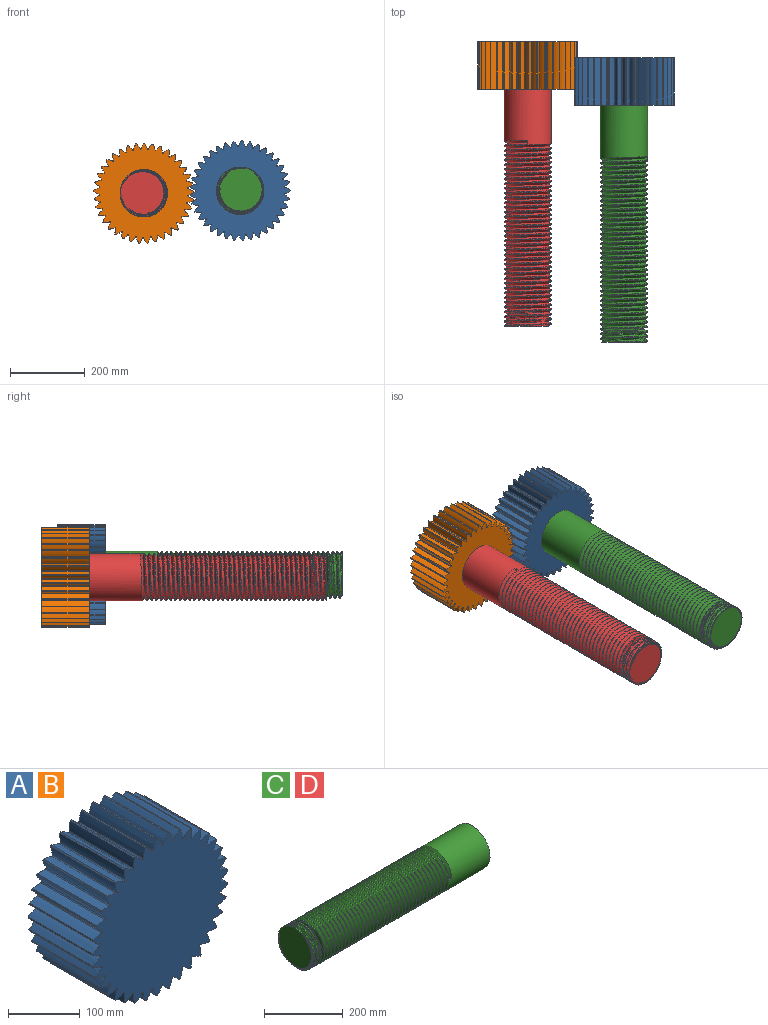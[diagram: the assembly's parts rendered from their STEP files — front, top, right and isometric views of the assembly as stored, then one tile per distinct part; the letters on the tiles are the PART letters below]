
ASSEMBLY  parts=4 mates=2
PART A: 150 faces, bbox 267.3x127x267.6 mm
  f0: cylinder r=133.86mm len=127mm, axis (0,1,0), area 302.8mm2, adj f139,f146,f148,f149
  f1: cylinder r=133.86mm len=127mm, axis (0,1,0), area 302.8mm2, adj f143,f145,f148,f149
  f2: cylinder r=133.86mm len=127mm, axis (0,1,0), area 302.8mm2, adj f136,f140,f148,f149
  f3: cylinder r=133.86mm len=127mm, axis (0,1,0), area 302.8mm2, adj f133,f137,f148,f149
  f4: cylinder r=133.86mm len=127mm, axis (0,1,0), area 302.8mm2, adj f130,f134,f148,f149
  f5: cylinder r=133.86mm len=127mm, axis (0,1,0), area 302.8mm2, adj f127,f131,f148,f149
  f6: cylinder r=133.86mm len=127mm, axis (0,1,0), area 302.8mm2, adj f124,f128,f148,f149
  f7: cylinder r=133.86mm len=127mm, axis (0,1,0), area 302.8mm2, adj f115,f125,f148,f149
  f8: cylinder r=133.86mm len=127mm, axis (0,1,0), area 302.8mm2, adj f109,f122,f148,f149
  f9: cylinder r=133.86mm len=127mm, axis (0,1,0), area 302.8mm2, adj f119,f121,f148,f149
  f10: cylinder r=133.86mm len=127mm, axis (0,1,0), area 302.8mm2, adj f112,f116,f148,f149
  f11: cylinder r=133.86mm len=127mm, axis (0,1,0), area 302.8mm2, adj f113,f118,f148,f149
  f12: cylinder r=133.86mm len=127mm, axis (0,1,0), area 302.8mm2, adj f106,f110,f148,f149
  f13: cylinder r=133.86mm len=127mm, axis (0,1,0), area 302.8mm2, adj f103,f107,f148,f149
  f14: cylinder r=133.86mm len=127mm, axis (0,1,0), area 302.8mm2, adj f100,f104,f148,f149
  f15: cylinder r=133.86mm len=127mm, axis (0,1,0), area 302.8mm2, adj f88,f101,f148,f149
  f16: cylinder r=133.86mm len=127mm, axis (0,1,0), area 302.8mm2, adj f94,f98,f148,f149
  f17: cylinder r=133.86mm len=127mm, axis (0,1,0), area 302.8mm2, adj f85,f95,f148,f149
  f18: cylinder r=133.86mm len=127mm, axis (0,1,0), area 302.8mm2, adj f92,f97,f148,f149
  f19: cylinder r=133.86mm len=127mm, axis (0,1,0), area 302.8mm2, adj f89,f91,f148,f149
  f20: cylinder r=133.86mm len=127mm, axis (0,1,0), area 302.8mm2, adj f82,f86,f148,f149
  f21: cylinder r=133.86mm len=127mm, axis (0,1,0), area 302.8mm2, adj f79,f83,f148,f149
  f22: cylinder r=133.86mm len=127mm, axis (0,1,0), area 302.8mm2, adj f76,f80,f148,f149
  f23: cylinder r=133.86mm len=127mm, axis (0,1,0), area 302.8mm2, adj f52,f77,f148,f149
  f24: cylinder r=133.86mm len=127mm, axis (0,1,0), area 302.8mm2, adj f37,f74,f148,f149
  f25: cylinder r=133.86mm len=127mm, axis (0,1,0), area 302.8mm2, adj f71,f73,f148,f149
  f26: cylinder r=133.86mm len=127mm, axis (0,1,0), area 302.8mm2, adj f64,f68,f148,f149
  f27: cylinder r=133.86mm len=127mm, axis (0,1,0), area 302.8mm2, adj f65,f70,f148,f149
  f28: cylinder r=133.86mm len=127mm, axis (0,1,0), area 302.8mm2, adj f58,f62,f148,f149
  f29: cylinder r=133.86mm len=127mm, axis (0,1,0), area 302.8mm2, adj f59,f67,f148,f149
  f30: cylinder r=133.86mm len=127mm, axis (0,1,0), area 302.8mm2, adj f56,f61,f148,f149
  f31: cylinder r=133.86mm len=127mm, axis (0,1,0), area 302.8mm2, adj f53,f55,f148,f149
  f32: cylinder r=133.86mm len=127mm, axis (0,1,0), area 302.8mm2, adj f46,f50,f148,f149
  f33: cylinder r=133.86mm len=127mm, axis (0,1,0), area 302.8mm2, adj f47,f142,f148,f149
  f34: cylinder r=133.86mm len=127mm, axis (0,1,0), area 302.8mm2, adj f44,f49,f148,f149
  f35: cylinder r=133.86mm len=127mm, axis (0,1,0), area 302.8mm2, adj f41,f43,f148,f149
  f36: cylinder r=133.86mm len=127mm, axis (0,1,0), area 302.8mm2, adj f38,f40,f148,f149
  f37: extruded ~127x14.19mm, area 2130.1mm2, adj f24,f39,f148,f149
  f38: extruded ~127x14.19mm, area 2130.1mm2, adj f36,f39,f148,f149
  f39: cylinder r=1.44mm len=127mm, axis (0,1,0), area 425.2mm2, adj f37,f38,f148,f149
  f40: extruded ~127x15.48mm, area 2130.1mm2, adj f36,f42,f148,f149
  f41: extruded ~127x12.49mm, area 2130.1mm2, adj f35,f42,f148,f149
  f42: cylinder r=1.44mm len=127mm, axis (0,1,0), area 425.2mm2, adj f40,f41,f148,f149
  f43: extruded ~127x16.33mm, area 2130.1mm2, adj f35,f45,f148,f149
  f44: extruded ~127x13.07mm, area 2130.1mm2, adj f34,f45,f148,f149
  f45: cylinder r=1.44mm len=127mm, axis (0,1,0), area 425.2mm2, adj f43,f44,f148,f149
  f46: extruded ~127x16.6mm, area 2130.1mm2, adj f32,f48,f148,f149
  f47: extruded ~127x15.8mm, area 2130.1mm2, adj f33,f48,f148,f149
  f48: cylinder r=1.44mm len=127mm, axis (0,1,0), area 425.2mm2, adj f46,f47,f148,f149
  f49: extruded ~127x16.7mm, area 2130.1mm2, adj f34,f51,f148,f149
  f50: extruded ~127x14.64mm, area 2130.1mm2, adj f32,f51,f148,f149
  f51: cylinder r=1.44mm len=127mm, axis (0,1,0), area 425.2mm2, adj f49,f50,f148,f149
  f52: extruded ~127x15.74mm, area 2130.1mm2, adj f23,f54,f148,f149
  f53: extruded ~127x12.01mm, area 2130.1mm2, adj f31,f54,f148,f149
  f54: cylinder r=1.44mm len=127mm, axis (0,1,0), area 425.2mm2, adj f52,f53,f148,f149
  f55: extruded ~127x16.47mm, area 2130.1mm2, adj f31,f57,f148,f149
  f56: extruded ~127x13.5mm, area 2130.1mm2, adj f30,f57,f148,f149
  f57: cylinder r=1.44mm len=127mm, axis (0,1,0), area 425.2mm2, adj f55,f56,f148,f149
  f58: extruded ~127x16.5mm, area 2130.1mm2, adj f28,f60,f148,f149
  f59: extruded ~127x16.01mm, area 2130.1mm2, adj f29,f60,f148,f149
  f60: cylinder r=1.44mm len=127mm, axis (0,1,0), area 425.2mm2, adj f58,f59,f148,f149
  f61: extruded ~127x16.72mm, area 2130.1mm2, adj f30,f63,f148,f149
  f62: extruded ~127x14.97mm, area 2130.1mm2, adj f28,f63,f148,f149
  f63: cylinder r=1.44mm len=127mm, axis (0,1,0), area 425.2mm2, adj f61,f62,f148,f149
  f64: extruded ~127x14.64mm, area 2130.1mm2, adj f26,f66,f148,f149
  f65: extruded ~127x16.7mm, area 2130.1mm2, adj f27,f66,f148,f149
  f66: cylinder r=1.44mm len=127mm, axis (0,1,0), area 425.2mm2, adj f64,f65,f148,f149
  f67: extruded ~127x15.8mm, area 2130.1mm2, adj f29,f69,f148,f149
  f68: extruded ~127x16.6mm, area 2130.1mm2, adj f26,f69,f148,f149
  f69: cylinder r=1.44mm len=127mm, axis (0,1,0), area 425.2mm2, adj f67,f68,f148,f149
  f70: extruded ~127x13.07mm, area 2130.1mm2, adj f27,f72,f148,f149
  f71: extruded ~127x16.33mm, area 2130.1mm2, adj f25,f72,f148,f149
  f72: cylinder r=1.44mm len=127mm, axis (0,1,0), area 425.2mm2, adj f70,f71,f148,f149
  f73: extruded ~127x12.49mm, area 2130.1mm2, adj f25,f75,f148,f149
  f74: extruded ~127x15.48mm, area 2130.1mm2, adj f24,f75,f148,f149
  f75: cylinder r=1.44mm len=127mm, axis (0,1,0), area 425.2mm2, adj f73,f74,f148,f149
  f76: extruded ~127x14.55mm, area 2130.1mm2, adj f22,f78,f148,f149
  f77: extruded ~127x13.8mm, area 2130.1mm2, adj f23,f78,f148,f149
  f78: cylinder r=1.44mm len=127mm, axis (0,1,0), area 425.2mm2, adj f76,f77,f148,f149
  f79: extruded ~127x12.95mm, area 2130.1mm2, adj f21,f81,f148,f149
  f80: extruded ~127x15.2mm, area 2130.1mm2, adj f22,f81,f148,f149
  f81: cylinder r=1.44mm len=127mm, axis (0,1,0), area 425.2mm2, adj f79,f80,f148,f149
  f82: extruded ~127x12.61mm, area 2130.1mm2, adj f20,f84,f148,f149
  f83: extruded ~127x16.16mm, area 2130.1mm2, adj f21,f84,f148,f149
  f84: cylinder r=1.44mm len=127mm, axis (0,1,0), area 425.2mm2, adj f82,f83,f148,f149
  f85: extruded ~127x14.28mm, area 2130.1mm2, adj f17,f87,f148,f149
  f86: extruded ~127x16.65mm, area 2130.1mm2, adj f20,f87,f148,f149
  f87: cylinder r=1.44mm len=127mm, axis (0,1,0), area 425.2mm2, adj f85,f86,f148,f149
  f88: extruded ~127x16.57mm, area 2130.1mm2, adj f15,f90,f148,f149
  f89: extruded ~127x13.9mm, area 2130.1mm2, adj f19,f90,f148,f149
  f90: cylinder r=1.44mm len=127mm, axis (0,1,0), area 425.2mm2, adj f88,f89,f148,f149
  f91: extruded ~127x16.71mm, area 2130.1mm2, adj f19,f93,f148,f149
  f92: extruded ~127x15.27mm, area 2130.1mm2, adj f18,f93,f148,f149
  f93: cylinder r=1.44mm len=127mm, axis (0,1,0), area 425.2mm2, adj f91,f92,f148,f149
  f94: extruded ~127x15.55mm, area 2130.1mm2, adj f16,f96,f148,f149
  f95: extruded ~127x16.67mm, area 2130.1mm2, adj f17,f96,f148,f149
  f96: cylinder r=1.44mm len=127mm, axis (0,1,0), area 425.2mm2, adj f94,f95,f148,f149
  f97: extruded ~127x16.36mm, area 2130.1mm2, adj f18,f99,f148,f149
  f98: extruded ~127x16.2mm, area 2130.1mm2, adj f16,f99,f148,f149
  f99: cylinder r=1.44mm len=127mm, axis (0,1,0), area 425.2mm2, adj f97,f98,f148,f149
  f100: extruded ~127x15.96mm, area 2130.1mm2, adj f14,f102,f148,f149
  f101: extruded ~127x12.13mm, area 2130.1mm2, adj f15,f102,f148,f149
  f102: cylinder r=1.44mm len=127mm, axis (0,1,0), area 425.2mm2, adj f100,f101,f148,f149
  f103: extruded ~127x14.89mm, area 2130.1mm2, adj f13,f105,f148,f149
  f104: extruded ~127x13.39mm, area 2130.1mm2, adj f14,f105,f148,f149
  f105: cylinder r=1.44mm len=127mm, axis (0,1,0), area 425.2mm2, adj f103,f104,f148,f149
  f106: extruded ~127x13.39mm, area 2130.1mm2, adj f12,f108,f148,f149
  f107: extruded ~127x14.89mm, area 2130.1mm2, adj f13,f108,f148,f149
  f108: cylinder r=1.44mm len=127mm, axis (0,1,0), area 425.2mm2, adj f106,f107,f148,f149
  f109: extruded ~127x12.13mm, area 2130.1mm2, adj f8,f111,f148,f149
  f110: extruded ~127x15.96mm, area 2130.1mm2, adj f12,f111,f148,f149
  f111: cylinder r=1.44mm len=127mm, axis (0,1,0), area 425.2mm2, adj f109,f110,f148,f149
  f112: extruded ~127x16.2mm, area 2130.1mm2, adj f10,f114,f148,f149
  f113: extruded ~127x16.36mm, area 2130.1mm2, adj f11,f114,f148,f149
  f114: cylinder r=1.44mm len=127mm, axis (0,1,0), area 425.2mm2, adj f112,f113,f148,f149
  f115: extruded ~127x16.67mm, area 2130.1mm2, adj f7,f117,f148,f149
  f116: extruded ~127x15.55mm, area 2130.1mm2, adj f10,f117,f148,f149
  f117: cylinder r=1.44mm len=127mm, axis (0,1,0), area 425.2mm2, adj f115,f116,f148,f149
  f118: extruded ~127x15.27mm, area 2130.1mm2, adj f11,f120,f148,f149
  f119: extruded ~127x16.71mm, area 2130.1mm2, adj f9,f120,f148,f149
  f120: cylinder r=1.44mm len=127mm, axis (0,1,0), area 425.2mm2, adj f118,f119,f148,f149
  f121: extruded ~127x13.9mm, area 2130.1mm2, adj f9,f123,f148,f149
  f122: extruded ~127x16.57mm, area 2130.1mm2, adj f8,f123,f148,f149
  f123: cylinder r=1.44mm len=127mm, axis (0,1,0), area 425.2mm2, adj f121,f122,f148,f149
  f124: extruded ~127x16.65mm, area 2130.1mm2, adj f6,f126,f148,f149
  f125: extruded ~127x14.28mm, area 2130.1mm2, adj f7,f126,f148,f149
  f126: cylinder r=1.44mm len=127mm, axis (0,1,0), area 425.2mm2, adj f124,f125,f148,f149
  f127: extruded ~127x16.16mm, area 2130.1mm2, adj f5,f129,f148,f149
  f128: extruded ~127x12.61mm, area 2130.1mm2, adj f6,f129,f148,f149
  f129: cylinder r=1.44mm len=127mm, axis (0,1,0), area 425.2mm2, adj f127,f128,f148,f149
  f130: extruded ~127x15.2mm, area 2130.1mm2, adj f4,f132,f148,f149
  f131: extruded ~127x12.95mm, area 2130.1mm2, adj f5,f132,f148,f149
  f132: cylinder r=1.44mm len=127mm, axis (0,1,0), area 425.2mm2, adj f130,f131,f148,f149
  f133: extruded ~127x13.8mm, area 2130.1mm2, adj f3,f135,f148,f149
  f134: extruded ~127x14.55mm, area 2130.1mm2, adj f4,f135,f148,f149
  f135: cylinder r=1.44mm len=127mm, axis (0,1,0), area 425.2mm2, adj f133,f134,f148,f149
  f136: extruded ~127x12.01mm, area 2130.1mm2, adj f2,f138,f148,f149
  f137: extruded ~127x15.74mm, area 2130.1mm2, adj f3,f138,f148,f149
  f138: cylinder r=1.44mm len=127mm, axis (0,1,0), area 425.2mm2, adj f136,f137,f148,f149
  f139: extruded ~127x13.5mm, area 2130.1mm2, adj f0,f141,f148,f149
  f140: extruded ~127x16.47mm, area 2130.1mm2, adj f2,f141,f148,f149
  f141: cylinder r=1.44mm len=127mm, axis (0,1,0), area 425.2mm2, adj f139,f140,f148,f149
  f142: extruded ~127x16.01mm, area 2130.1mm2, adj f33,f144,f148,f149
  f143: extruded ~127x16.5mm, area 2130.1mm2, adj f1,f144,f148,f149
  f144: cylinder r=1.44mm len=127mm, axis (0,1,0), area 425.2mm2, adj f142,f143,f148,f149
  f145: extruded ~127x14.97mm, area 2130.1mm2, adj f1,f147,f148,f149
  f146: extruded ~127x16.72mm, area 2130.1mm2, adj f0,f147,f148,f149
  f147: cylinder r=1.44mm len=127mm, axis (0,1,0), area 425.2mm2, adj f145,f146,f148,f149
  f148: plane 267.59x267.35mm, normal (0,-1,0), area 50480.1mm2, adj f0,f1,f2,f3,f4,f5,f6,f7
  f149: plane 267.59x267.35mm, normal (0,1,0), area 50480.1mm2, adj f0,f1,f2,f3,f4,f5,f6,f7
PART B: same geometry as A
PART C: 45 faces, bbox 649.3x134.9x134.9 mm
  f0: cylinder r=63.5mm len=52.68mm, axis (-1,0,0), area 61.2mm2, adj f1,f40,f43
  f1: cylinder r=63.5mm len=127mm, axis (-1,0,0), area 785.3mm2, adj f0,f2,f42,f43
  f2: cylinder r=63.5mm len=127mm, axis (-1,0,0), area 784.7mm2, adj f1,f3,f42,f43
  f3: cylinder r=63.5mm len=127mm, axis (-1,0,0), area 784.6mm2, adj f2,f4,f42,f43
  f4: cylinder r=63.5mm len=127mm, axis (-1,0,0), area 784.9mm2, adj f3,f5,f42,f43
  f5: cylinder r=63.5mm len=127mm, axis (-1,0,0), area 785.4mm2, adj f4,f6,f42,f43
  f6: cylinder r=63.5mm len=127mm, axis (-1,0,0), area 786.1mm2, adj f5,f7,f42,f43
  f7: cylinder r=63.5mm len=127mm, axis (-1,0,0), area 786.7mm2, adj f6,f8,f42,f43
  f8: cylinder r=63.5mm len=127mm, axis (-1,0,0), area 787.1mm2, adj f7,f9,f42,f43
  f9: cylinder r=63.5mm len=127mm, axis (-1,0,0), area 787.2mm2, adj f8,f10,f42,f43
  f10: cylinder r=63.5mm len=127mm, axis (-1,0,0), area 787mm2, adj f9,f11,f42,f43
  f11: cylinder r=63.5mm len=127mm, axis (-1,0,0), area 786.3mm2, adj f10,f12,f42,f43
  f12: cylinder r=63.5mm len=127mm, axis (-1,0,0), area 785.7mm2, adj f11,f13,f42,f43
  f13: cylinder r=63.5mm len=127mm, axis (-1,0,0), area 785.3mm2, adj f12,f14,f42,f43
  f14: cylinder r=63.5mm len=127mm, axis (-1,0,0), area 785.2mm2, adj f13,f15,f42,f43
  f15: cylinder r=63.5mm len=127mm, axis (-1,0,0), area 785.3mm2, adj f14,f16,f42,f43
  f16: cylinder r=63.5mm len=127mm, axis (-1,0,0), area 785.5mm2, adj f15,f17,f42,f43
  f17: cylinder r=63.5mm len=127mm, axis (-1,0,0), area 785.7mm2, adj f16,f18,f42,f43
  f18: cylinder r=63.5mm len=127mm, axis (-1,0,0), area 785.8mm2, adj f17,f19,f42,f43
  f19: cylinder r=63.5mm len=127mm, axis (-1,0,0), area 785.8mm2, adj f18,f20,f42,f43
  f20: cylinder r=63.5mm len=127mm, axis (-1,0,0), area 785.7mm2, adj f19,f21,f42,f43
  f21: cylinder r=63.5mm len=127mm, axis (-1,0,0), area 785.3mm2, adj f20,f22,f42,f43
  f22: cylinder r=63.5mm len=127mm, axis (-1,0,0), area 785.1mm2, adj f21,f23,f42,f43
  f23: cylinder r=63.5mm len=127mm, axis (-1,0,0), area 785.4mm2, adj f22,f24,f42,f43
  f24: cylinder r=63.5mm len=127mm, axis (-1,0,0), area 785.8mm2, adj f23,f25,f42,f43
  f25: cylinder r=63.5mm len=127mm, axis (-1,0,0), area 786.3mm2, adj f24,f26,f42,f43
  f26: cylinder r=63.5mm len=127mm, axis (-1,0,0), area 786.7mm2, adj f25,f27,f42,f43
  f27: cylinder r=63.5mm len=127mm, axis (-1,0,0), area 787mm2, adj f26,f28,f42,f43
  f28: cylinder r=63.5mm len=127mm, axis (-1,0,0), area 787mm2, adj f27,f29,f42,f43
  f29: cylinder r=63.5mm len=127mm, axis (-1,0,0), area 786.8mm2, adj f28,f30,f42,f43
  f30: cylinder r=63.5mm len=127mm, axis (-1,0,0), area 786.3mm2, adj f29,f31,f42,f43
  f31: cylinder r=63.5mm len=127mm, axis (-1,0,0), area 785.5mm2, adj f30,f32,f42,f43
  f32: cylinder r=63.5mm len=127mm, axis (-1,0,0), area 784.9mm2, adj f31,f33,f42,f43
  f33: cylinder r=63.5mm len=127mm, axis (-1,0,0), area 784.7mm2, adj f32,f34,f42,f43
  f34: cylinder r=63.5mm len=127mm, axis (-1,0,0), area 784.8mm2, adj f33,f35,f42,f43
  f35: cylinder r=63.5mm len=127mm, axis (-1,0,0), area 785mm2, adj f34,f36,f42,f43
  f36: cylinder r=63.5mm len=127mm, axis (-1,0,0), area 785.4mm2, adj f35,f37,f42,f43
  f37: cylinder r=63.5mm len=127mm, axis (-1,0,0), area 785.8mm2, adj f36,f38,f42,f43
  f38: cylinder r=63.5mm len=127mm, axis (-1,0,0), area 786.2mm2, adj f37,f39,f42,f43
  f39: cylinder r=63.5mm len=152.4mm, axis (-1,0,0), area 57201.7mm2, adj f38,f41,f42,f43,f44
  f40: plane 126.72x125.41mm, normal (-1,0,0), area 11181.9mm2, adj f0,f42,f43
  f41: plane 10.73x9.26mm, normal (0,0,1), area 49.7mm2, adj f39,f42,f43
  f42: bspline ~506.03x127mm, area 159068.4mm2, adj f1,f2,f3,f4,f5,f6,f7,f8
  f43: bspline ~498.75x128.07mm, area 148804.9mm2, adj f0,f1,f2,f3,f4,f5,f6,f7
  f44: plane 127x127mm, normal (1,0,0), area 12667.7mm2, adj f39
PART D: same geometry as C
PLACE A rot(axis=(0,-1,0),131.7deg) t=(49.64,-104.51,-122.76)mm
PLACE B rot(axis=(0,-1,0),123.4deg) t=(-208.49,-61.95,-129.37)mm
PLACE C rot(axis=(0.13,0.13,0.98),91deg) t=(49.64,-803.01,-122.76)mm fixed
PLACE D rot(axis=(-0.58,-0.58,0.58),120deg) t=(-208.49,-760.45,-129.37)mm fixed
MATE revolute A.f0 <-> C.f0  axis (0,-1,0) through (49.64,-168.01,-122.76)mm
MATE revolute D.f0 <-> B.f0  axis (0,-1,0) through (-208.49,-125.45,-129.37)mm
